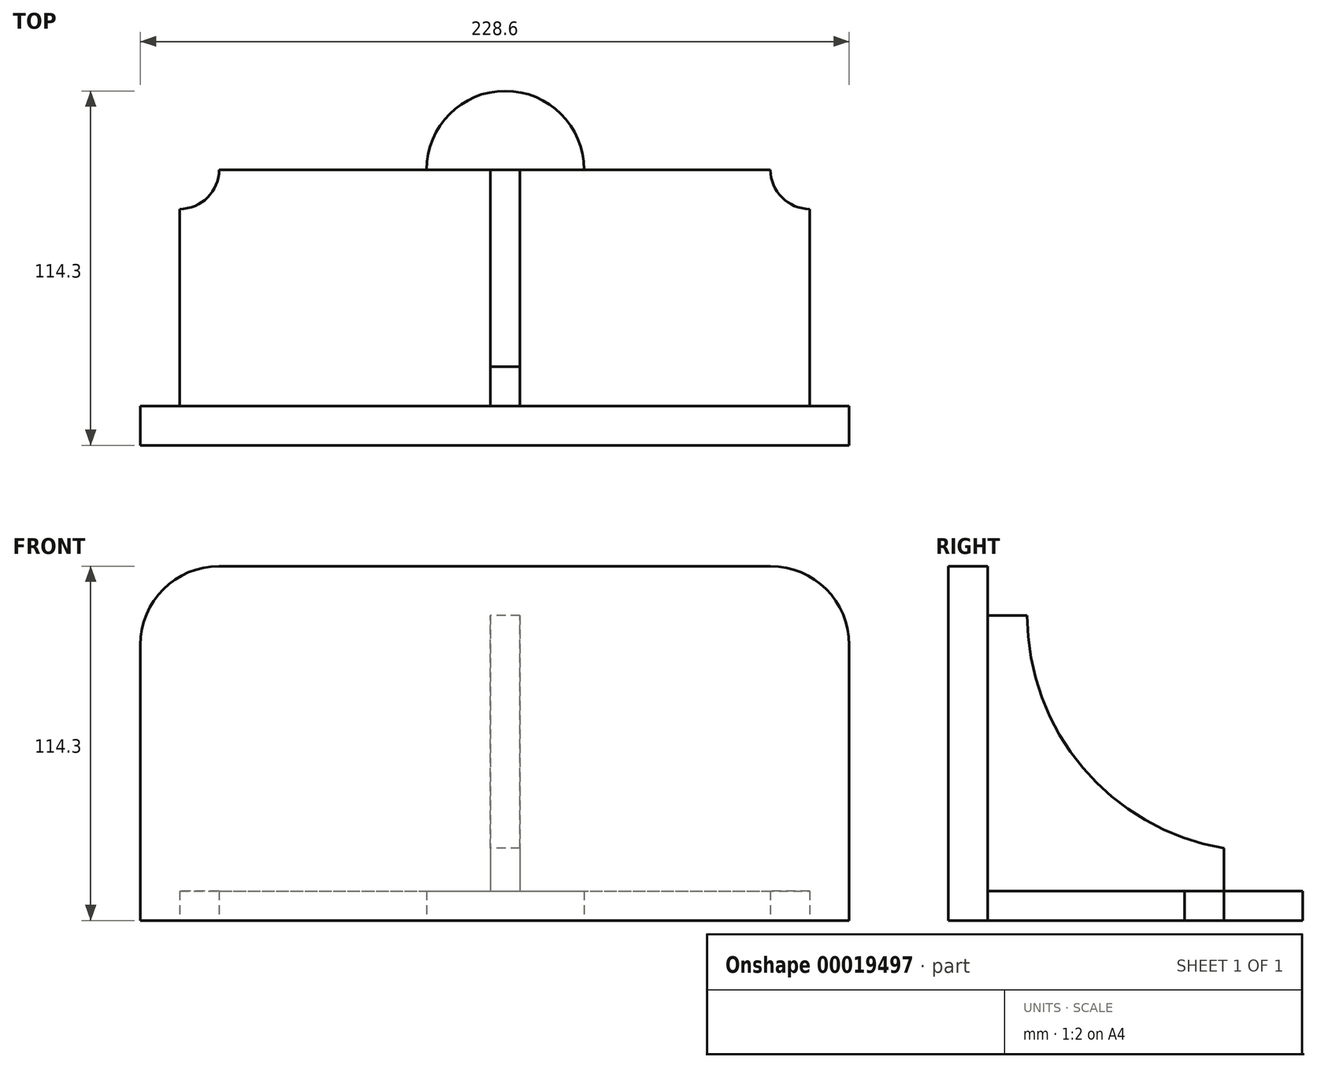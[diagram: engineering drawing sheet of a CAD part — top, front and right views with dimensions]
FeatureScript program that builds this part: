
annotation { "Feature Type Name" : "Feature", "Feature Type Description" : "" }
export const myFeature = defineFeature(function(context is Context, id is Id, definition is map)
    precondition{}
    {
        {
            var Q0;
            Q0=qCreatedBy(makeId("Front.planeOp"),FACE);
            var sketch = newSketch(context, id + "F0", { "sketchPlane" : qUnion([Q0])});
            skLineSegment(sketch, "E0.bottom", {"start": v(-92.3, 73.77) * mm, "end": v(85.5, 73.77) * mm});
            skLineSegment(sketch, "E0.top", {"start": v(-117.7, -40.53) * mm, "end": v(110.9, -40.53) * mm});
            skLineSegment(sketch, "E0.left", {"start": v(-117.7, 48.37) * mm, "end": v(-117.7, -40.53) * mm});
            skLineSegment(sketch, "E0.right", {"start": v(110.9, 48.37) * mm, "end": v(110.9, -40.53) * mm});
            skPoint(sketch, "E1.visualSharp", {"position": v(-117.7, 73.77) * mm});
            skArc(sketch, "E1.filletArc", {"start": v(-92.3, 73.77) * mm, "mid": v(-110.25, 66.33) * mm, "end": v(-117.7, 48.37) * mm});
            skPoint(sketch, "E2.visualSharp", {"position": v(110.9, 73.77) * mm});
            skArc(sketch, "E2.filletArc", {"start": v(110.9, 48.37) * mm, "mid": v(103.47, 66.33) * mm, "end": v(85.5, 73.77) * mm});
            skSolve(sketch);
        }
        {
            var Q0;
            Q0=makeQuery(id+"F0.imprint","IMPRINT",FACE,{"disambiguationData":[TD([[makeQuery(id+"F0.imprint","IMPRINT",EDGE,{"derivedFrom":sQuery(id+"F0.wireOp",EDGE,"E0.bottom")}),-1.0]])]});
            extrude(context, id + "F1", {"entities" : qUnion([Q0]), "depth" : 12.7 * mm});
        }
        {
            var Q0;
            Q0=makeQuery(id+"F1.opExtrude","SWEPT_FACE",FACE,{"disambiguationData":[OSD([sQuery(id+"F0.wireOp",EDGE,"E0.top")])]});
            var sketch = newSketch(context, id + "F2", { "sketchPlane" : qUnion([Q0])});
            skLineSegment(sketch, "E3.bottom", {"start": v(-105, 12.7) * mm, "end": v(98.2, 12.7) * mm});
            skLineSegment(sketch, "E3.left", {"start": v(-105, 12.7) * mm, "end": v(-105, -63.5) * mm});
            skLineSegment(sketch, "E3.right", {"start": v(98.2, 12.7) * mm, "end": v(98.2, -63.5) * mm});
            skArc(sketch, "E4", {"start": v(-92.3, -76.2) * mm, "mid": v(-96.01, -67.22) * mm, "end": v(-105, -63.5) * mm});
            skLineSegment(sketch, "E5", {"start": v(-92.3, -76.2) * mm, "end": v(85.5, -76.2) * mm});
            skArc(sketch, "E6", {"start": v(98.2, -63.5) * mm, "mid": v(89.23, -67.22) * mm, "end": v(85.5, -76.2) * mm});
            skSolve(sketch);
        }
        {
            var Q0;
            {var subQ6=sQuery(id+"F2.wireOp",EDGE,"E4");Q0=makeQuery(id+"F2.imprint","IMPRINT",FACE,{"disambiguationData":[TD([[makeQuery(id+"F2.imprint","IMPRINT",EDGE,{"derivedFrom":subQ6}),-1.0]])]});}
            extrude(context, id + "F3", {"entities" : qUnion([Q0]), "oppositeDirection" : true, "depth" : 9.52 * mm});
        }
        {
            var Q0;
            Q0=makeQuery(id+"F3.opExtrude","CAP_FACE",FACE,{"disambiguationData":[OSD([sQuery(id+"F0.wireOp",EDGE,"E0.top"),sQuery(id+"F2.wireOp",EDGE,"E3.left"),sQuery(id+"F2.wireOp",EDGE,"E3.right"),sQuery(id+"F2.wireOp",EDGE,"E4"),sQuery(id+"F2.wireOp",EDGE,"E5"),sQuery(id+"F2.wireOp",EDGE,"E6")])],"isStart":true});
            var sketch = newSketch(context, id + "F4", { "sketchPlane" : qUnion([Q0])});
            skArc(sketch, "E7", {"start": v(-25.4, -76.2) * mm, "mid": v(0, -101.6) * mm, "end": v(25.4, -76.2) * mm});
            skLineSegment(sketch, "E8", {"start": v(-25.4, -76.2) * mm, "end": v(25.4, -76.2) * mm});
            skSolve(sketch);
        }
        {
            var Q0;
            Q0=makeQuery(id+"F4.imprint","IMPRINT",FACE,{"disambiguationData":[TD([[makeQuery(id+"F4.imprint","IMPRINT",EDGE,{"derivedFrom":sQuery(id+"F4.wireOp",EDGE,"E7")}),1.0]])]});
            extrude(context, id + "F5", {"entities" : qUnion([Q0]), "oppositeDirection" : true, "depth" : 9.52 * mm});
        }
        {
            var Q0;
            Q0=makeQuery(id+"F3.opExtrude","CAP_FACE",FACE,{"disambiguationData":[OSD([sQuery(id+"F0.wireOp",EDGE,"E0.top"),sQuery(id+"F2.wireOp",EDGE,"E3.left"),sQuery(id+"F2.wireOp",EDGE,"E3.right"),sQuery(id+"F2.wireOp",EDGE,"E4"),sQuery(id+"F2.wireOp",EDGE,"E5"),sQuery(id+"F2.wireOp",EDGE,"E6")])],"isStart":false});
            var sketch = newSketch(context, id + "F6", { "sketchPlane" : qUnion([Q0])});
            skLineSegment(sketch, "E9.bottom", {"start": v(4.76, 0) * mm, "end": v(-4.76, 0) * mm});
            skLineSegment(sketch, "E9.top", {"start": v(4.76, 76.2) * mm, "end": v(-4.76, 76.2) * mm});
            skLineSegment(sketch, "E9.left", {"start": v(4.76, 0) * mm, "end": v(4.76, 76.2) * mm});
            skLineSegment(sketch, "E9.right", {"start": v(-4.76, 0) * mm, "end": v(-4.76, 76.2) * mm});
            skSolve(sketch);
        }
        {
            var Q0;
            Q0=makeQuery(id+"F6.imprint","IMPRINT",FACE,{"disambiguationData":[TD([[makeQuery(id+"F6.imprint","IMPRINT",EDGE,{"derivedFrom":sQuery(id+"F6.wireOp",EDGE,"E9.bottom")}),1.0]])]});
            extrude(context, id + "F7", {"entities" : qUnion([Q0]), "depth" : 88.9 * mm});
        }
        {
            var Q0;
            Q0=makeQuery(id+"F7.opExtrude","SWEPT_FACE",FACE,{"disambiguationData":[OSD([sQuery(id+"F6.wireOp",EDGE,"E9.right")])]});
            var sketch = newSketch(context, id + "F8", { "sketchPlane" : qUnion([Q0])});
            skLineSegment(sketch, "E10", {"start": v(-76.2, 57.9) * mm, "end": v(-88.9, 57.9) * mm});
            skArc(sketch, "E11", {"start": v(-76.2, -17.24) * mm, "mid": v(-30.7, 8.7) * mm, "end": v(-12.7, 57.9) * mm});
            skSolve(sketch);
        }
        {
            var Q0;
            Q0 = qSketchRegion(id + "F8", true);
            var Q1;
            {var subQ0=sQuery(id+"F6.wireOp",EDGE,"E9.right");var subQ1=makeQuery(id+"F7.opExtrude","CAP_EDGE",EDGE,{"disambiguationData":[OSD([subQ0])],"isStart":false});var subQ2=sQuery(id+"F8.wireOp",EDGE,"E11");var subQ3=makeQuery(id+"F8.imprint","INTERSECT",VERTEX,{"derivedFrom":[subQ1,subQ2]});Q1=makeQuery(id+"F8.imprint","IMPRINT",FACE,{"disambiguationData":[TD([[makeQuery(id+"F8.imprint","IMPRINT",EDGE,{"disambiguationData":[TD([[subQ3,1.0]])],"derivedFrom":subQ2}),1.0]])]});}
            extrude(context, id + "F9", {"entities" : qUnion([Q0, Q1]), "operationType" : NewBodyOperationType.REMOVE, "oppositeDirection" : true, "depth" : 9.52 * mm});
        }
    });
